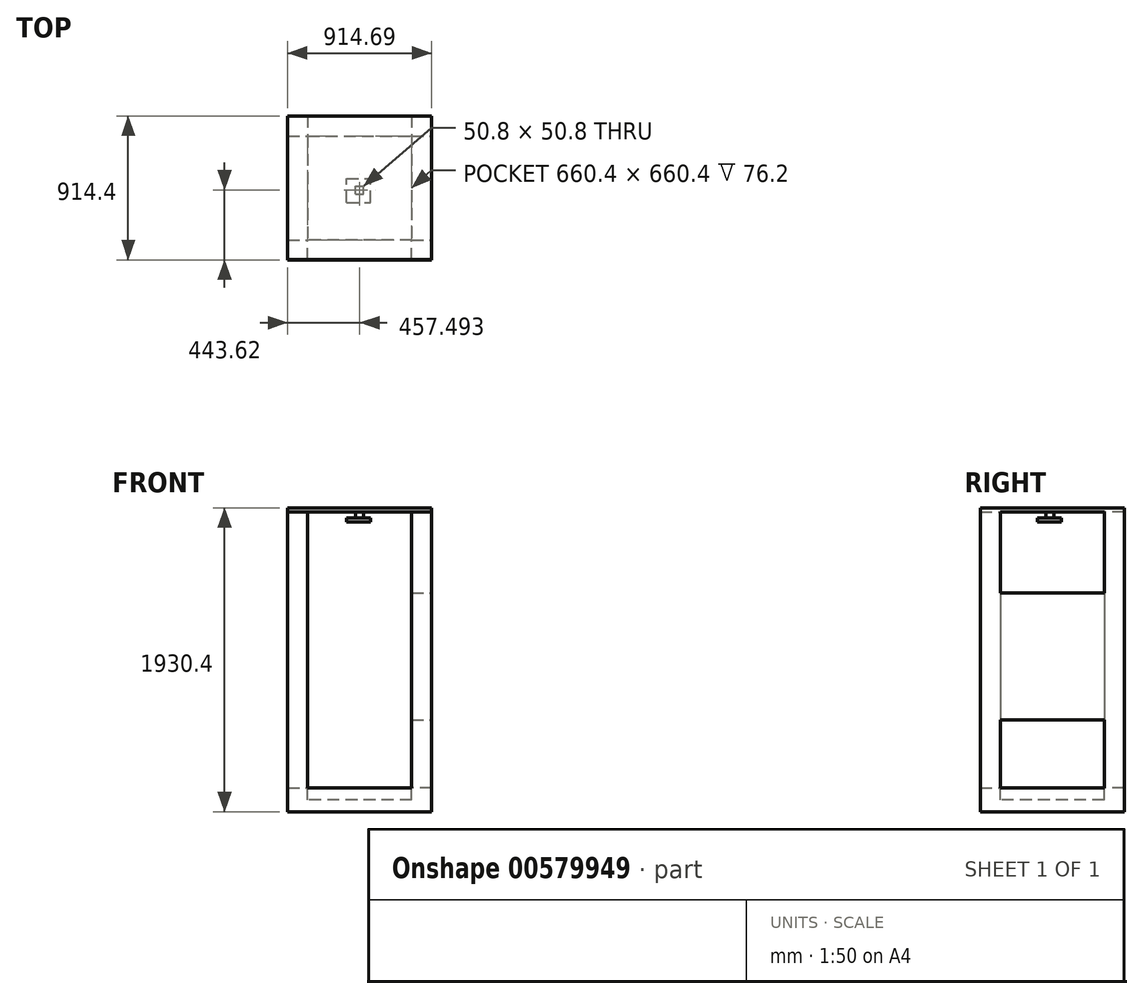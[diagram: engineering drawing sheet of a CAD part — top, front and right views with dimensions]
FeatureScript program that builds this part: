
annotation { "Feature Type Name" : "Feature", "Feature Type Description" : "" }
export const myFeature = defineFeature(function(context is Context, id is Id, definition is map)
    precondition{}
    {
        {
            var Q0;
            Q0=qCreatedBy(makeId("Top.planeOp"),FACE);
            var sketch = newSketch(context, id + "F0", { "sketchPlane" : qUnion([Q0])});
            skLineSegment(sketch, "E0.bottom", {"start": v(-479.92, 445.38) * mm, "end": v(434.48, 445.38) * mm});
            skLineSegment(sketch, "E0.top", {"start": v(-479.92, -469.02) * mm, "end": v(434.48, -469.02) * mm});
            skLineSegment(sketch, "E0.left", {"start": v(-479.92, 445.38) * mm, "end": v(-479.92, -469.02) * mm});
            skLineSegment(sketch, "E0.right", {"start": v(434.48, 445.38) * mm, "end": v(434.48, -469.02) * mm});
            skSolve(sketch);
        }
        {
            var Q0;
            Q0=makeQuery(id+"F0.imprint","IMPRINT",FACE,{"disambiguationData":[TD([[makeQuery(id+"F0.imprint","IMPRINT",EDGE,{"derivedFrom":sQuery(id+"F0.wireOp",EDGE,"E0.bottom")}),-1.0]])]});
            extrude(context, id + "F1", {"entities" : qUnion([Q0]), "depth" : 76.2 * mm, "offsetDistance" : 25.4 * mm});
        }
        {
            var Q0;
            Q0=makeQuery(id+"F1.opExtrude","CAP_FACE",FACE,{"disambiguationData":[OSD([sQuery(id+"F0.wireOp",EDGE,"E0.bottom"),sQuery(id+"F0.wireOp",EDGE,"E0.top"),sQuery(id+"F0.wireOp",EDGE,"E0.left"),sQuery(id+"F0.wireOp",EDGE,"E0.right")])],"isStart":false});
            var sketch = newSketch(context, id + "F2", { "sketchPlane" : qUnion([Q0])});
            skLineSegment(sketch, "E1.bottom", {"start": v(-479.92, 445.38) * mm, "end": v(-352.92, 445.38) * mm});
            skLineSegment(sketch, "E1.top", {"start": v(-479.92, 318.38) * mm, "end": v(-352.92, 318.38) * mm});
            skLineSegment(sketch, "E1.left", {"start": v(-479.92, 445.38) * mm, "end": v(-479.92, 318.38) * mm});
            skLineSegment(sketch, "E1.right", {"start": v(-352.92, 445.38) * mm, "end": v(-352.92, 318.38) * mm});
            skLineSegment(sketch, "E2.bottom", {"start": v(434.48, 445.38) * mm, "end": v(307.48, 445.38) * mm});
            skLineSegment(sketch, "E2.top", {"start": v(434.48, 318.38) * mm, "end": v(307.48, 318.38) * mm});
            skLineSegment(sketch, "E2.left", {"start": v(434.48, 445.38) * mm, "end": v(434.48, 318.38) * mm});
            skLineSegment(sketch, "E2.right", {"start": v(307.48, 445.38) * mm, "end": v(307.48, 318.38) * mm});
            skLineSegment(sketch, "E3.bottom", {"start": v(434.48, -469.02) * mm, "end": v(307.48, -469.02) * mm});
            skLineSegment(sketch, "E3.top", {"start": v(434.48, -342.02) * mm, "end": v(307.48, -342.02) * mm});
            skLineSegment(sketch, "E3.left", {"start": v(434.48, -469.02) * mm, "end": v(434.48, -342.02) * mm});
            skLineSegment(sketch, "E3.right", {"start": v(307.48, -469.02) * mm, "end": v(307.48, -342.02) * mm});
            skLineSegment(sketch, "E4.bottom", {"start": v(-479.92, -469.02) * mm, "end": v(-352.92, -469.02) * mm});
            skLineSegment(sketch, "E4.top", {"start": v(-479.92, -342.02) * mm, "end": v(-352.92, -342.02) * mm});
            skLineSegment(sketch, "E4.left", {"start": v(-479.92, -469.02) * mm, "end": v(-479.92, -342.02) * mm});
            skLineSegment(sketch, "E4.right", {"start": v(-352.92, -469.02) * mm, "end": v(-352.92, -342.02) * mm});
            skSolve(sketch);
        }
        {
            var Q0;
            Q0 = qSketchRegion(id + "F2", true);
            extrude(context, id + "F3", {"entities" : qUnion([Q0]), "operationType" : NewBodyOperationType.ADD, "depth" : 1828.8 * mm, "offsetDistance" : 25.4 * mm});
        }
        {
            var Q0;
            Q0=makeQuery(id+"F3.opExtrude","CAP_FACE",FACE,{"disambiguationData":[OSD([sQuery(id+"F2.wireOp",EDGE,"E2.bottom"),sQuery(id+"F2.wireOp",EDGE,"E2.top"),sQuery(id+"F2.wireOp",EDGE,"E2.left"),sQuery(id+"F2.wireOp",EDGE,"E2.right")])],"isStart":false});
            var sketch = newSketch(context, id + "F4", { "sketchPlane" : qUnion([Q0])});
            skLineSegment(sketch, "E5.bottom", {"start": v(434.48, 445.38) * mm, "end": v(-480.21, 445.38) * mm});
            skLineSegment(sketch, "E5.top", {"start": v(434.48, -467.94) * mm, "end": v(-480.21, -467.94) * mm});
            skLineSegment(sketch, "E5.left", {"start": v(434.48, 445.38) * mm, "end": v(434.48, -467.94) * mm});
            skLineSegment(sketch, "E5.right", {"start": v(-480.21, 445.38) * mm, "end": v(-480.21, -467.94) * mm});
            skSolve(sketch);
        }
        {
            var Q0;
            Q0 = qSketchRegion(id + "F4", true);
            extrude(context, id + "F5", {"entities" : qUnion([Q0]), "operationType" : NewBodyOperationType.ADD, "depth" : 25.4 * mm, "offsetDistance" : 25.4 * mm});
        }
        {
            var Q0;
            Q0=makeQuery(id+"F3.opExtrude","SWEPT_FACE",FACE,{"disambiguationData":[OSD([sQuery(id+"F2.wireOp",EDGE,"E1.top")])]});
            var sketch = newSketch(context, id + "F6", { "sketchPlane" : qUnion([Q0])});
            skLineSegment(sketch, "E6.bottom", {"start": v(-479.92, 76.2) * mm, "end": v(-352.92, 76.2) * mm});
            skLineSegment(sketch, "E6.top", {"start": v(-479.92, 152.4) * mm, "end": v(-352.92, 152.4) * mm});
            skLineSegment(sketch, "E6.left", {"start": v(-479.92, 76.2) * mm, "end": v(-479.92, 152.4) * mm});
            skLineSegment(sketch, "E6.right", {"start": v(-352.92, 76.2) * mm, "end": v(-352.92, 152.4) * mm});
            skSolve(sketch);
        }
        {
            var Q0;
            Q0=makeQuery(id+"F6.imprint","IMPRINT",FACE,{"disambiguationData":[TD([[makeQuery(id+"F6.imprint","IMPRINT",EDGE,{"derivedFrom":sQuery(id+"F6.wireOp",EDGE,"E6.bottom")}),1.0]])]});
            extrude(context, id + "F7", {"entities" : qUnion([Q0]), "operationType" : NewBodyOperationType.ADD, "depth" : 660.4 * mm, "offsetDistance" : 25.4 * mm});
        }
        {
            var Q0;
            Q0=makeQuery(id+"F7.boolean.opBoolean","MERGE",FACE,{"derivedFrom":[makeQuery(id+"F3.opExtrude","SWEPT_FACE",FACE,{"disambiguationData":[OSD([sQuery(id+"F2.wireOp",EDGE,"E1.right")])]}),makeQuery(id+"F3.opExtrude","SWEPT_FACE",FACE,{"disambiguationData":[OSD([sQuery(id+"F2.wireOp",EDGE,"E4.right")])]}),makeQuery(id+"F7.opExtrude","SWEPT_FACE",FACE,{"disambiguationData":[OSD([sQuery(id+"F6.wireOp",EDGE,"E6.right")])]})]});
            var sketch = newSketch(context, id + "F8", { "sketchPlane" : qUnion([Q0])});
            skLineSegment(sketch, "E7.bottom", {"start": v(-469.02, 76.2) * mm, "end": v(-342.02, 76.2) * mm});
            skLineSegment(sketch, "E7.top", {"start": v(-469.02, 152.4) * mm, "end": v(-342.02, 152.4) * mm});
            skLineSegment(sketch, "E7.left", {"start": v(-469.02, 76.2) * mm, "end": v(-469.02, 152.4) * mm});
            skLineSegment(sketch, "E7.right", {"start": v(-342.02, 76.2) * mm, "end": v(-342.02, 152.4) * mm});
            skSolve(sketch);
        }
        {
            var Q0;
            Q0=makeQuery(id+"F8.imprint","IMPRINT",FACE,{"disambiguationData":[TD([[makeQuery(id+"F8.imprint","IMPRINT",EDGE,{"derivedFrom":sQuery(id+"F8.wireOp",EDGE,"E7.bottom")}),-1.0]])]});
            extrude(context, id + "F9", {"entities" : qUnion([Q0]), "operationType" : NewBodyOperationType.ADD, "depth" : 660.4 * mm, "offsetDistance" : 25.4 * mm});
        }
        {
            var Q0;
            Q0=makeQuery(id+"F9.boolean.opBoolean","MERGE",FACE,{"derivedFrom":[makeQuery(id+"F3.opExtrude","SWEPT_FACE",FACE,{"disambiguationData":[OSD([sQuery(id+"F2.wireOp",EDGE,"E3.top")])]}),makeQuery(id+"F9.opExtrude","SWEPT_FACE",FACE,{"disambiguationData":[OSD([sQuery(id+"F8.wireOp",EDGE,"E7.right")])]})]});
            var sketch = newSketch(context, id + "F10", { "sketchPlane" : qUnion([Q0])});
            skLineSegment(sketch, "E8.bottom", {"start": v(-434.48, 76.2) * mm, "end": v(-307.48, 76.2) * mm});
            skLineSegment(sketch, "E8.top", {"start": v(-434.48, 152.4) * mm, "end": v(-307.48, 152.4) * mm});
            skLineSegment(sketch, "E8.left", {"start": v(-434.48, 76.2) * mm, "end": v(-434.48, 152.4) * mm});
            skLineSegment(sketch, "E8.right", {"start": v(-307.48, 76.2) * mm, "end": v(-307.48, 152.4) * mm});
            skSolve(sketch);
        }
        {
            var Q0;
            Q0=makeQuery(id+"F10.imprint","IMPRINT",FACE,{"disambiguationData":[TD([[makeQuery(id+"F10.imprint","IMPRINT",EDGE,{"derivedFrom":sQuery(id+"F10.wireOp",EDGE,"E8.bottom")}),1.0]])]});
            extrude(context, id + "F11", {"entities" : qUnion([Q0]), "operationType" : NewBodyOperationType.ADD, "depth" : 660.4 * mm, "offsetDistance" : 25.4 * mm});
        }
        {
            var Q0;
            Q0=makeQuery(id+"F11.boolean.opBoolean","MERGE",FACE,{"derivedFrom":[makeQuery(id+"F3.opExtrude","SWEPT_FACE",FACE,{"disambiguationData":[OSD([sQuery(id+"F2.wireOp",EDGE,"E2.right")])]}),makeQuery(id+"F11.opExtrude","SWEPT_FACE",FACE,{"disambiguationData":[OSD([sQuery(id+"F10.wireOp",EDGE,"E8.right")])]})]});
            var sketch = newSketch(context, id + "F12", { "sketchPlane" : qUnion([Q0])});
            skLineSegment(sketch, "E9.bottom", {"start": v(-445.38, 76.2) * mm, "end": v(-318.38, 76.2) * mm});
            skLineSegment(sketch, "E9.top", {"start": v(-445.38, 152.4) * mm, "end": v(-318.38, 152.4) * mm});
            skLineSegment(sketch, "E9.left", {"start": v(-445.38, 76.2) * mm, "end": v(-445.38, 152.4) * mm});
            skLineSegment(sketch, "E9.right", {"start": v(-318.38, 76.2) * mm, "end": v(-318.38, 152.4) * mm});
            skSolve(sketch);
        }
        {
            var Q0;
            Q0=makeQuery(id+"F12.imprint","IMPRINT",FACE,{"disambiguationData":[TD([[makeQuery(id+"F12.imprint","IMPRINT",EDGE,{"derivedFrom":sQuery(id+"F12.wireOp",EDGE,"E9.bottom")}),1.0]])]});
            extrude(context, id + "F13", {"entities" : qUnion([Q0]), "operationType" : NewBodyOperationType.ADD, "depth" : 660.4 * mm, "offsetDistance" : 25.4 * mm});
        }
        {
            var Q0;
            Q0=makeQuery(id+"F5.opExtrude","CAP_FACE",FACE,{"disambiguationData":[OSD([sQuery(id+"F4.wireOp",EDGE,"E5.bottom"),sQuery(id+"F4.wireOp",EDGE,"E5.top"),sQuery(id+"F4.wireOp",EDGE,"E5.left"),sQuery(id+"F4.wireOp",EDGE,"E5.right")])],"isStart":true});
            var sketch = newSketch(context, id + "F14", { "sketchPlane" : qUnion([Q0])});
            skLineSegment(sketch, "E10.bottom", {"start": v(-48.12, 50.8) * mm, "end": v(2.68, 50.8) * mm});
            skLineSegment(sketch, "E10.top", {"start": v(-48.12, 0) * mm, "end": v(2.68, 0) * mm});
            skLineSegment(sketch, "E10.left", {"start": v(-48.12, 50.8) * mm, "end": v(-48.12, 0) * mm});
            skLineSegment(sketch, "E10.right", {"start": v(2.68, 50.8) * mm, "end": v(2.68, 0) * mm});
            skSolve(sketch);
        }
        {
            var Q0;
            Q0=makeQuery(id+"F14.imprint","IMPRINT",FACE,{"disambiguationData":[TD([[makeQuery(id+"F14.imprint","IMPRINT",EDGE,{"derivedFrom":sQuery(id+"F14.wireOp",EDGE,"E10.bottom")}),-1.0]])]});
            extrude(context, id + "F15", {"entities" : qUnion([Q0]), "operationType" : NewBodyOperationType.ADD, "depth" : 63.5 * mm, "offsetDistance" : 25.4 * mm});
        }
        {
            var Q0;
            Q0=makeQuery(id+"F15.opExtrude","CAP_FACE",FACE,{"disambiguationData":[OSD([sQuery(id+"F14.wireOp",EDGE,"E10.bottom"),sQuery(id+"F14.wireOp",EDGE,"E10.top"),sQuery(id+"F14.wireOp",EDGE,"E10.left"),sQuery(id+"F14.wireOp",EDGE,"E10.right")])],"isStart":false});
            var sketch = newSketch(context, id + "F16", { "sketchPlane" : qUnion([Q0])});
            skLineSegment(sketch, "E11.bottom", {"start": v(-105.97, 105.43) * mm, "end": v(46.43, 105.43) * mm});
            skLineSegment(sketch, "E11.top", {"start": v(-105.97, -46.97) * mm, "end": v(46.43, -46.97) * mm});
            skLineSegment(sketch, "E11.left", {"start": v(-105.97, 105.43) * mm, "end": v(-105.97, -46.97) * mm});
            skLineSegment(sketch, "E11.right", {"start": v(46.43, 105.43) * mm, "end": v(46.43, -46.97) * mm});
            skSolve(sketch);
        }
        {
            var Q0;
            Q0=makeQuery(id+"F16.imprint","IMPRINT",FACE,{"disambiguationData":[TD([[makeQuery(id+"F16.imprint","IMPRINT",EDGE,{"derivedFrom":sQuery(id+"F16.wireOp",EDGE,"E11.bottom")}),-1.0]])]});
            extrude(context, id + "F17", {"entities" : qUnion([Q0]), "operationType" : NewBodyOperationType.ADD, "oppositeDirection" : true, "depth" : 25.4 * mm, "offsetDistance" : 25.4 * mm});
        }
        {
            var Q0;
            Q0=makeQuery(id+"F3.opExtrude","SWEPT_FACE",FACE,{"disambiguationData":[OSD([sQuery(id+"F2.wireOp",EDGE,"E2.top")])]});
            var sketch = newSketch(context, id + "F18", { "sketchPlane" : qUnion([Q0])});
            skLineSegment(sketch, "E12.bottom", {"start": v(307.48, 1390.2) * mm, "end": v(434.48, 1390.2) * mm});
            skLineSegment(sketch, "E12.top", {"start": v(307.48, 582.22) * mm, "end": v(434.48, 582.22) * mm});
            skLineSegment(sketch, "E12.left", {"start": v(307.48, 1390.2) * mm, "end": v(307.48, 582.22) * mm});
            skLineSegment(sketch, "E12.right", {"start": v(434.48, 1390.2) * mm, "end": v(434.48, 582.22) * mm});
            skSolve(sketch);
        }
        {
            var Q0;
            Q0 = qSketchRegion(id + "F18", true);
            extrude(context, id + "F19", {"entities" : qUnion([Q0]), "operationType" : NewBodyOperationType.ADD, "depth" : 660.4 * mm, "offsetDistance" : 25.4 * mm});
        }
    });
